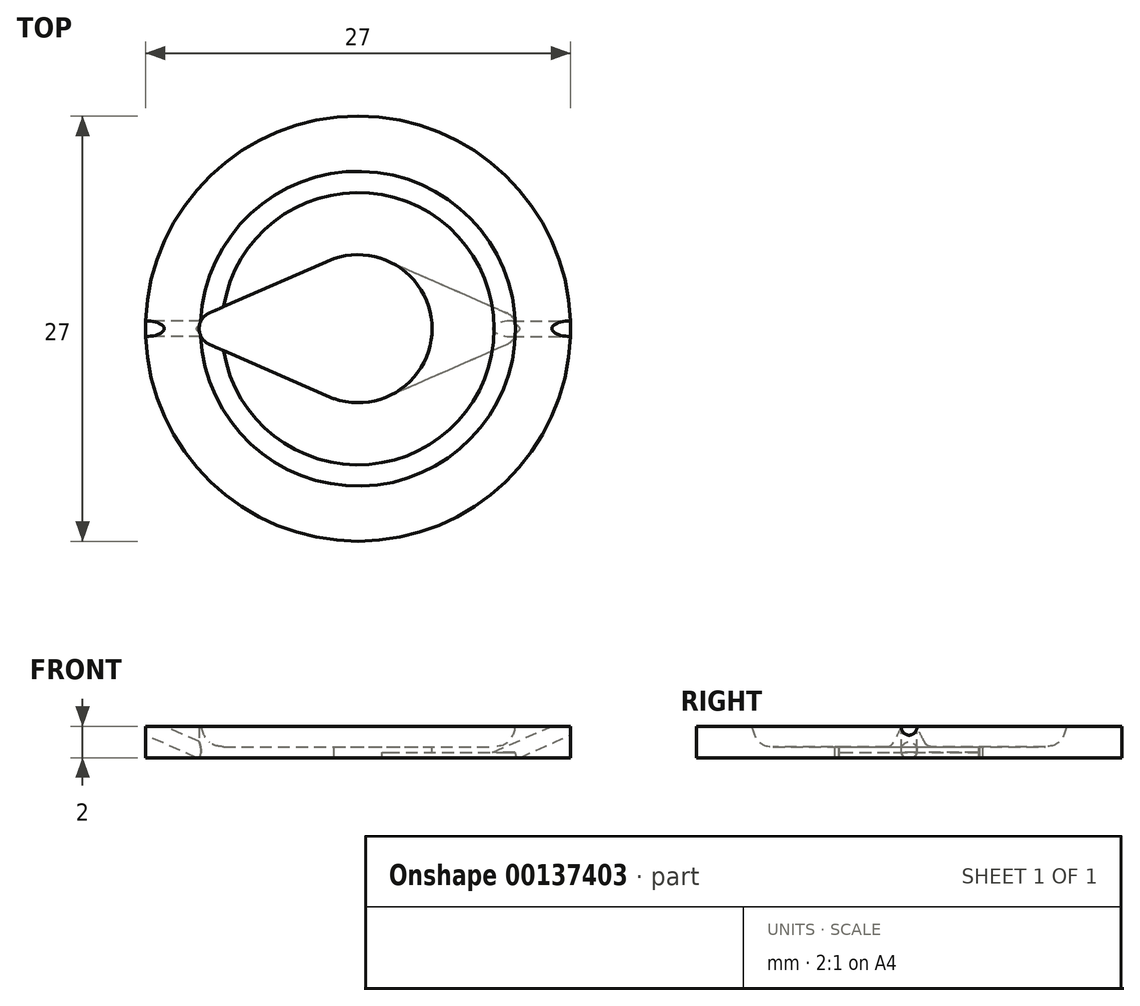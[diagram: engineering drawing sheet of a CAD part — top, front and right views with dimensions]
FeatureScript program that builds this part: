
annotation { "Feature Type Name" : "Feature", "Feature Type Description" : "" }
export const myFeature = defineFeature(function(context is Context, id is Id, definition is map)
    precondition{}
    {
        {
            var Q0;
            Q0=qCreatedBy(makeId("Front.planeOp"),FACE);
            var sketch = newSketch(context, id + "F0", { "sketchPlane" : qUnion([Q0])});
            skLineSegment(sketch, "E0", {"start": v(-10, 2) * mm, "end": v(-13.5, 2) * mm});
            skLineSegment(sketch, "E1", {"start": v(-13.5, 2) * mm, "end": v(-13.5, 0) * mm});
            skLineSegment(sketch, "E2", {"start": v(-13.5, 0) * mm, "end": v(-4.7, 0) * mm});
            skLineSegment(sketch, "E3", {"start": v(-4.7, 0) * mm, "end": v(-4.7, 0.7) * mm});
            skLineSegment(sketch, "E4", {"start": v(-4.7, 0.7) * mm, "end": v(-8.65, 0.7) * mm});
            skFitSpline(sketch, "E5", {"points": [v(-10, 2) * mm, v(-8.65, 0.7) * mm], "startDerivative": vector(0.56, -2.2) * mm, "endDerivative": vector(2.85, -0.07) * mm});
            skLineSegment(sketch, "E6", {"start": v(0, 14.08) * mm, "end": v(0, -13.4) * mm});
            skSolve(sketch);
        }
        {
            var Q0;
            Q0=makeQuery(id+"F0.imprint","IMPRINT",FACE,{"disambiguationData":[TD([[makeQuery(id+"F0.imprint","IMPRINT",EDGE,{"derivedFrom":sQuery(id+"F0.wireOp",EDGE,"E0")}),1.0]])]});
            var Q1;
            Q1=sQuery(id+"F0.wireOp",EDGE,"E6");
            revolve(context, id + "F1", {"entities" : qUnion([Q0]), "axis" : qUnion([Q1]), "revolveType" : RevolveType.FULL});
        }
        {
            var Q0;
            Q0=qCreatedBy(makeId("Top.planeOp"),FACE);
            var sketch = newSketch(context, id + "F2", { "sketchPlane" : qUnion([Q0])});
            skLineSegment(sketch, "E7", {"start": v(1.53, 4.46) * mm, "end": v(9.44, 1) * mm});
            skLineSegment(sketch, "E8.MirrorCS", {"start": v(1.53, -4.46) * mm, "end": v(9.44, -1) * mm});
            skArc(sketch, "E9", {"start": v(9.44, -1) * mm, "mid": v(10.1, 0) * mm, "end": v(9.44, 1) * mm});
            skLineSegment(sketch, "E10.MirrorCS", {"start": v(-1.53, 4.46) * mm, "end": v(-9.44, 1) * mm});
            skArc(sketch, "E11.MirrorCS", {"start": v(-9.44, -1) * mm, "mid": v(-10.1, 0) * mm, "end": v(-9.44, 1) * mm});
            skLineSegment(sketch, "E12.MirrorCS", {"start": v(-1.53, -4.46) * mm, "end": v(-9.44, -1) * mm});
            skLineSegment(sketch, "E13", {"start": v(1.53, -4.46) * mm, "end": v(1.53, 4.46) * mm});
            skLineSegment(sketch, "E14", {"start": v(-1.53, -4.46) * mm, "end": v(-1.53, 4.46) * mm});
            skSolve(sketch);
        }
        {
            var Q0;
            Q0=makeQuery(id+"F2.imprint","IMPRINT",FACE,{"disambiguationData":[TD([[makeQuery(id+"F2.imprint","IMPRINT",EDGE,{"derivedFrom":sQuery(id+"F2.wireOp",EDGE,"E7")}),-1.0]])]});
            extrude(context, id + "F3", {"entities" : qUnion([Q0]), "operationType" : NewBodyOperationType.REMOVE, "depth" : 0.35 * mm});
        }
        {
            var Q0;
            Q0=makeQuery(id+"F2.imprint","IMPRINT",FACE,{"disambiguationData":[TD([[makeQuery(id+"F2.imprint","IMPRINT",EDGE,{"derivedFrom":sQuery(id+"F2.wireOp",EDGE,"E10.MirrorCS")}),1.0]])]});
            extrude(context, id + "F4", {"entities" : qUnion([Q0]), "operationType" : NewBodyOperationType.REMOVE, "depth" : 5 * mm});
        }
        {
            var Q0;
            Q0=qCreatedBy(makeId("Front.planeOp"),FACE);
            var sketch = newSketch(context, id + "F5", { "sketchPlane" : qUnion([Q0])});
            skLineSegment(sketch, "E15", {"start": v(9, 0) * mm, "end": v(13.55, 2) * mm});
            skLineSegment(sketch, "E16", {"start": v(7.85, 0.04) * mm, "end": v(13.38, 2.47) * mm});
            skLineSegment(sketch, "E17", {"start": v(7.85, 0.04) * mm, "end": v(9, 0) * mm});
            skLineSegment(sketch, "E18", {"start": v(13.55, 2) * mm, "end": v(13.38, 2.47) * mm});
            skLineSegment(sketch, "E19.MirrorCS", {"start": v(-13.55, 2) * mm, "end": v(-13.38, 2.47) * mm});
            skLineSegment(sketch, "E20.MirrorCS", {"start": v(-7.85, 0.04) * mm, "end": v(-13.38, 2.47) * mm});
            skLineSegment(sketch, "E21.MirrorCS", {"start": v(-9, 0) * mm, "end": v(-13.55, 2) * mm});
            skLineSegment(sketch, "E22.MirrorCS", {"start": v(-7.85, 0.04) * mm, "end": v(-9, 0) * mm});
            skSolve(sketch);
        }
        {
            var Q0;
            Q0=makeQuery(id+"F5.imprint","IMPRINT",FACE,{"disambiguationData":[TD([[makeQuery(id+"F5.imprint","IMPRINT",EDGE,{"derivedFrom":sQuery(id+"F5.wireOp",EDGE,"E15")}),1.0]])]});
            var Q1;
            Q1=sQuery(id+"F5.wireOp",EDGE,"E15");
            revolve(context, id + "F6", {"operationType" : NewBodyOperationType.REMOVE, "entities" : qUnion([Q0]), "axis" : qUnion([Q1]), "revolveType" : RevolveType.FULL, "oppositeDirection" : true});
        }
        {
            var Q0;
            Q0=makeQuery(id+"F5.imprint","IMPRINT",FACE,{"disambiguationData":[TD([[makeQuery(id+"F5.imprint","IMPRINT",EDGE,{"derivedFrom":sQuery(id+"F5.wireOp",EDGE,"E19.MirrorCS")}),-1.0]])]});
            var Q1;
            Q1=sQuery(id+"F5.wireOp",EDGE,"E21.MirrorCS");
            revolve(context, id + "F7", {"operationType" : NewBodyOperationType.REMOVE, "entities" : qUnion([Q0]), "axis" : qUnion([Q1]), "revolveType" : RevolveType.FULL, "oppositeDirection" : true});
        }
    });
